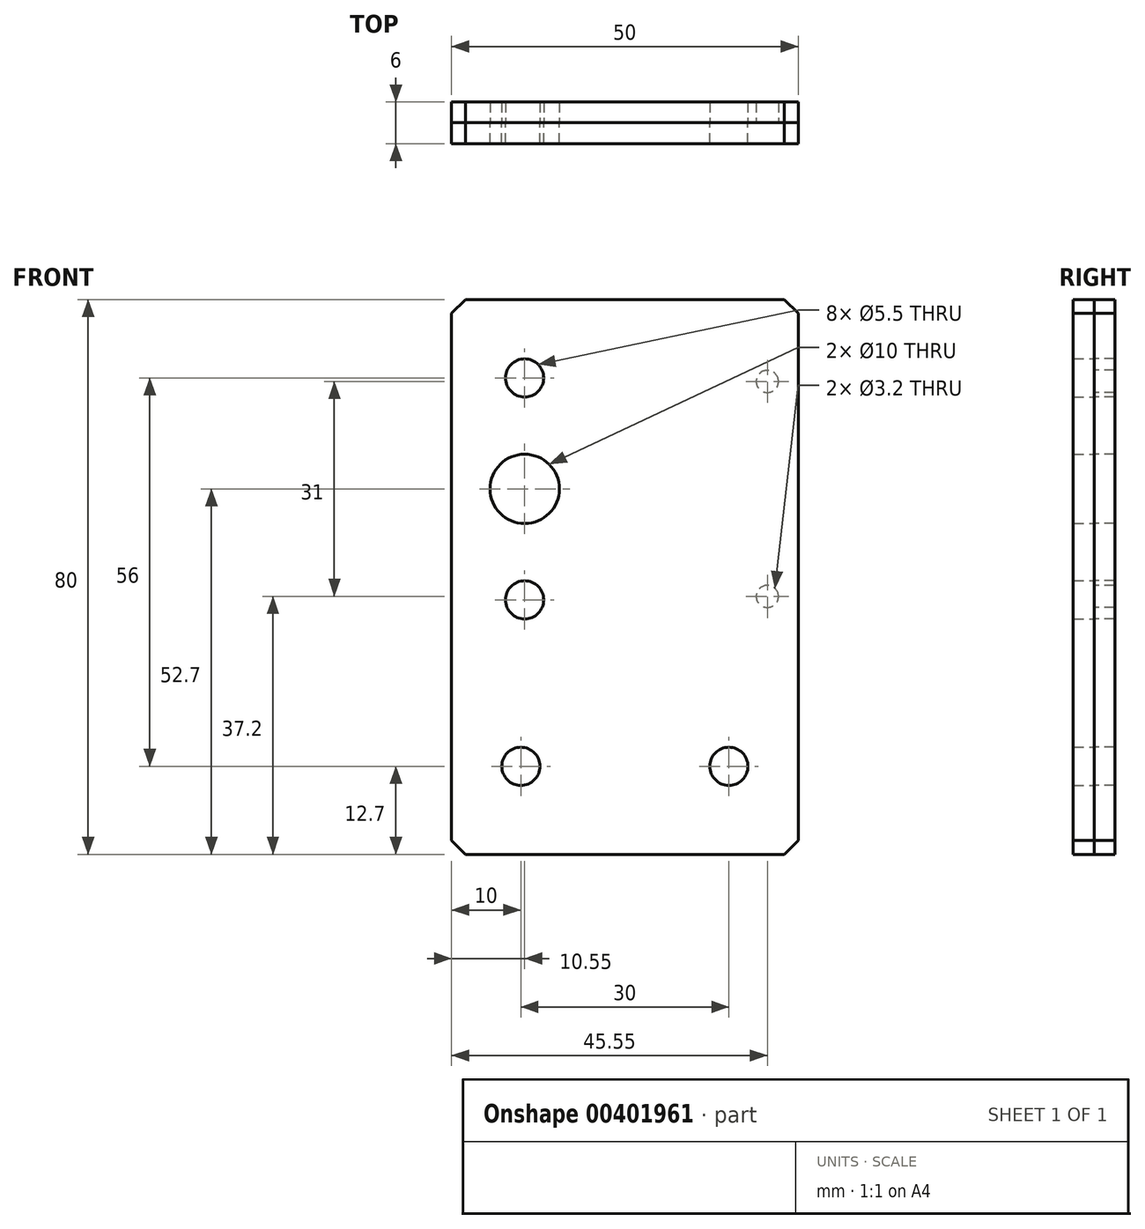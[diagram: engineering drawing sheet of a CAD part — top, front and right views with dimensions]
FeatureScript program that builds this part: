
annotation { "Feature Type Name" : "Feature", "Feature Type Description" : "" }
export const myFeature = defineFeature(function(context is Context, id is Id, definition is map)
    precondition{}
    {
        {
            var Q0;
            Q0=qCreatedBy(makeId("Front.planeOp"),FACE);
            var sketch = newSketch(context, id + "F0", { "sketchPlane" : qUnion([Q0])});
            skLineSegment(sketch, "E0.bottom", {"start": v(-25, 40) * mm, "end": v(25, 40) * mm});
            skLineSegment(sketch, "E0.top", {"start": v(-25, -40) * mm, "end": v(25, -40) * mm});
            skLineSegment(sketch, "E0.left", {"start": v(-25, 40) * mm, "end": v(-25, -40) * mm});
            skLineSegment(sketch, "E0.right", {"start": v(25, 40) * mm, "end": v(25, -40) * mm});
            skLineSegment(sketch, "E1", {"start": v(0, 0) * mm, "end": v(0, 40) * mm, "construction": true});
            skLineSegment(sketch, "E2", {"start": v(0, 0) * mm, "end": v(-25, 0) * mm, "construction": true});
            skSolve(sketch);
        }
        {
            var Q0;
            Q0=makeQuery(id+"F0.imprint","IMPRINT",FACE,{"disambiguationData":[TD([[makeQuery(id+"F0.imprint","IMPRINT",EDGE,{"derivedFrom":sQuery(id+"F0.wireOp",EDGE,"E0.bottom")}),-1.0]])]});
            extrude(context, id + "F1", {"entities" : qUnion([Q0]), "endBound" : BoundingType.SYMMETRIC, "depth" : 3 * mm});
        }
        {
            var Q0;
            Q0=makeQuery(id+"F1.opExtrude","CAP_FACE",FACE,{"disambiguationData":[OSD([sQuery(id+"F0.wireOp",EDGE,"E0.bottom"),sQuery(id+"F0.wireOp",EDGE,"E0.top"),sQuery(id+"F0.wireOp",EDGE,"E0.left"),sQuery(id+"F0.wireOp",EDGE,"E0.right")])],"isStart":false});
            var sketch = newSketch(context, id + "F2", { "sketchPlane" : qUnion([Q0])});
            skLineSegment(sketch, "E3", {"start": v(-25, -14.6) * mm, "end": v(25, -14.6) * mm, "construction": true});
            skPoint(sketch, "E4", {"position": v(-15, -27.3) * mm});
            skPoint(sketch, "E5", {"position": v(15, -27.3) * mm});
            skLineSegment(sketch, "E6", {"start": v(-15, -27.3) * mm, "end": v(15, -27.3) * mm, "construction": true});
            skLineSegment(sketch, "E7", {"start": v(15, -27.3) * mm, "end": v(25, -27.3) * mm, "construction": true});
            skLineSegment(sketch, "E8", {"start": v(-15, -27.3) * mm, "end": v(-25, -27.3) * mm, "construction": true});
            skPoint(sketch, "E9", {"position": v(20.55, 28.2) * mm});
            skPoint(sketch, "E10", {"position": v(20.55, -2.8) * mm});
            skLineSegment(sketch, "E11", {"start": v(20.55, 28.2) * mm, "end": v(20.55, 40) * mm, "construction": true});
            skLineSegment(sketch, "E12", {"start": v(20.55, -2.8) * mm, "end": v(20.55, -14.6) * mm, "construction": true});
            skLineSegment(sketch, "E13", {"start": v(20.55, 28.2) * mm, "end": v(20.55, -2.8) * mm, "construction": true});
            skLineSegment(sketch, "E14", {"start": v(20.55, 12.7) * mm, "end": v(-14.45, 12.7) * mm, "construction": true});
            skLineSegment(sketch, "E15", {"start": v(-14.45, 12.7) * mm, "end": v(-14.45, 28.7) * mm, "construction": true});
            skLineSegment(sketch, "E16", {"start": v(-14.45, 12.7) * mm, "end": v(-14.45, -3.3) * mm, "construction": true});
            skSolve(sketch);
        }
        {
            var Q0;
            Q0=sQuery(id+"F2.wireOp",VERTEX,"E4");
            var Q1;
            Q1=sQuery(id+"F2.wireOp",VERTEX,"E5");
            var Q2;
            Q2=makeQuery(id+"F1.opExtrude","SWEPT_BODY",BODY,{"disambiguationData":[OSD([sQuery(id+"F0.wireOp",EDGE,"E0.bottom"),sQuery(id+"F0.wireOp",EDGE,"E0.top"),sQuery(id+"F0.wireOp",EDGE,"E0.left"),sQuery(id+"F0.wireOp",EDGE,"E0.right")])]});
            hole(context, id + "F3", {"style" : HoleStyle.SIMPLE, "endStyle" : HoleEndStyle.THROUGH, "holeDiameter" : 5.5 * mm, "isTappedThrough" : true, "tappedDepth" : 12 * mm, "tapClearance" : 3, "locations" : qUnion([Q0, Q1]), "scope" : qUnion([Q2])});
        }
        {
            var Q0;
            Q0=sQuery(id+"F2.wireOp",VERTEX,"E9");
            var Q1;
            Q1=sQuery(id+"F2.wireOp",VERTEX,"E10");
            var Q2;
            Q2=makeQuery(id+"F1.opExtrude","SWEPT_BODY",BODY,{"disambiguationData":[OSD([sQuery(id+"F0.wireOp",EDGE,"E0.bottom"),sQuery(id+"F0.wireOp",EDGE,"E0.top"),sQuery(id+"F0.wireOp",EDGE,"E0.left"),sQuery(id+"F0.wireOp",EDGE,"E0.right")])]});
            hole(context, id + "F4", {"style" : HoleStyle.SIMPLE, "endStyle" : HoleEndStyle.THROUGH, "holeDiameter" : 3.2 * mm, "isTappedThrough" : true, "tappedDepth" : 12 * mm, "tapClearance" : 3, "locations" : qUnion([Q0, Q1]), "scope" : qUnion([Q2])});
        }
        {
            var Q0;
            Q0=makeQuery(id+"F1.opExtrude","SWEPT_EDGE",EDGE,{"disambiguationData":[OSD([sQuery(id+"F0.wireOp",EDGE,"E0.bottom"),sQuery(id+"F0.wireOp",EDGE,"E0.left")])]});
            var Q1;
            Q1=makeQuery(id+"F1.opExtrude","SWEPT_EDGE",EDGE,{"disambiguationData":[OSD([sQuery(id+"F0.wireOp",EDGE,"E0.top"),sQuery(id+"F0.wireOp",EDGE,"E0.left")])]});
            var Q2;
            Q2=makeQuery(id+"F1.opExtrude","SWEPT_EDGE",EDGE,{"disambiguationData":[OSD([sQuery(id+"F0.wireOp",EDGE,"E0.bottom"),sQuery(id+"F0.wireOp",EDGE,"E0.right")])]});
            var Q3;
            Q3=makeQuery(id+"F1.opExtrude","SWEPT_EDGE",EDGE,{"disambiguationData":[OSD([sQuery(id+"F0.wireOp",EDGE,"E0.top"),sQuery(id+"F0.wireOp",EDGE,"E0.right")])]});
            chamfer(context, id + "F5", {"entities" : qUnion([Q0, Q1, Q2, Q3]), "width" : 2 * mm, "tangentPropagation" : true});
        }
        {
            var Q0;
            Q0=sQuery(id+"F2.wireOp",VERTEX,"E15.end");
            var Q1;
            Q1=sQuery(id+"F2.wireOp",VERTEX,"E16.end");
            var Q2;
            Q2=makeQuery(id+"F1.opExtrude","SWEPT_BODY",BODY,{"disambiguationData":[OSD([sQuery(id+"F0.wireOp",EDGE,"E0.bottom"),sQuery(id+"F0.wireOp",EDGE,"E0.top"),sQuery(id+"F0.wireOp",EDGE,"E0.left"),sQuery(id+"F0.wireOp",EDGE,"E0.right")])]});
            hole(context, id + "F6", {"style" : HoleStyle.SIMPLE, "endStyle" : HoleEndStyle.THROUGH, "holeDiameter" : 5.5 * mm, "isTappedThrough" : true, "tappedDepth" : 12 * mm, "tapClearance" : 3, "locations" : qUnion([Q0, Q1]), "scope" : qUnion([Q2])});
        }
        {
            var Q0;
            Q0=sQuery(id+"F2.wireOp",VERTEX,"E15.start");
            var Q1;
            Q1=makeQuery(id+"F1.opExtrude","SWEPT_BODY",BODY,{"disambiguationData":[OSD([sQuery(id+"F0.wireOp",EDGE,"E0.bottom"),sQuery(id+"F0.wireOp",EDGE,"E0.top"),sQuery(id+"F0.wireOp",EDGE,"E0.left"),sQuery(id+"F0.wireOp",EDGE,"E0.right")])]});
            hole(context, id + "F7", {"style" : HoleStyle.SIMPLE, "endStyle" : HoleEndStyle.THROUGH, "holeDiameter" : 10 * mm, "isTappedThrough" : true, "tappedDepth" : 12 * mm, "tapClearance" : 3, "locations" : qUnion([Q0]), "scope" : qUnion([Q1])});
        }
        {
            var Q0;
            Q0=makeQuery(id+"F2.imprint","IMPRINT",FACE,{"disambiguationData":[TD([[makeQuery(id+"F2.imprint","IMPRINT",EDGE,{"derivedFrom":makeQuery(id+"F1.opExtrude","CAP_EDGE",EDGE,{"disambiguationData":[OSD([sQuery(id+"F0.wireOp",EDGE,"E0.bottom")])],"isStart":false})}),-1.0]])]});
            extrude(context, id + "F8", {"entities" : qUnion([Q0]), "depth" : 3 * mm});
        }
        {
            var Q0;
            Q0=makeQuery(id+"F8.opExtrude","SWEPT_EDGE",EDGE,{"disambiguationData":[OSD([sQuery(id+"F0.wireOp",EDGE,"E0.bottom"),sQuery(id+"F0.wireOp",EDGE,"E0.right")])]});
            var Q1;
            Q1=makeQuery(id+"F8.opExtrude","SWEPT_EDGE",EDGE,{"disambiguationData":[OSD([sQuery(id+"F0.wireOp",EDGE,"E0.bottom"),sQuery(id+"F0.wireOp",EDGE,"E0.left")])]});
            var Q2;
            Q2=makeQuery(id+"F8.opExtrude","SWEPT_EDGE",EDGE,{"disambiguationData":[OSD([sQuery(id+"F0.wireOp",EDGE,"E0.top"),sQuery(id+"F0.wireOp",EDGE,"E0.right")])]});
            var Q3;
            Q3=makeQuery(id+"F8.opExtrude","SWEPT_EDGE",EDGE,{"disambiguationData":[OSD([sQuery(id+"F0.wireOp",EDGE,"E0.top"),sQuery(id+"F0.wireOp",EDGE,"E0.left")])]});
            chamfer(context, id + "F9", {"entities" : qUnion([Q0, Q1, Q2, Q3]), "width" : 2 * mm, "tangentPropagation" : true});
        }
        {
            var Q0;
            Q0=sQuery(id+"F2.wireOp",VERTEX,"E5");
            var Q1;
            Q1=sQuery(id+"F2.wireOp",VERTEX,"E4");
            var Q2;
            Q2=makeQuery(id+"F8.opExtrude","SWEPT_BODY",BODY,{"disambiguationData":[OSD([sQuery(id+"F0.wireOp",EDGE,"E0.bottom"),sQuery(id+"F0.wireOp",EDGE,"E0.top"),sQuery(id+"F0.wireOp",EDGE,"E0.left"),sQuery(id+"F0.wireOp",EDGE,"E0.right")])]});
            hole(context, id + "F10", {"style" : HoleStyle.SIMPLE, "endStyle" : HoleEndStyle.THROUGH, "oppositeDirection" : true, "holeDiameter" : 5.5 * mm, "isTappedThrough" : true, "tappedDepth" : 12 * mm, "tapClearance" : 3, "locations" : qUnion([Q0, Q1]), "scope" : qUnion([Q2])});
        }
        {
            var Q0;
            Q0=sQuery(id+"F2.wireOp",VERTEX,"E15.end");
            var Q1;
            Q1=sQuery(id+"F2.wireOp",VERTEX,"E16.end");
            var Q2;
            Q2=makeQuery(id+"F8.opExtrude","SWEPT_BODY",BODY,{"disambiguationData":[OSD([sQuery(id+"F0.wireOp",EDGE,"E0.bottom"),sQuery(id+"F0.wireOp",EDGE,"E0.top"),sQuery(id+"F0.wireOp",EDGE,"E0.left"),sQuery(id+"F0.wireOp",EDGE,"E0.right")])]});
            hole(context, id + "F11", {"style" : HoleStyle.SIMPLE, "endStyle" : HoleEndStyle.THROUGH, "oppositeDirection" : true, "holeDiameter" : 5.5 * mm, "isTappedThrough" : true, "tappedDepth" : 12 * mm, "tapClearance" : 3, "locations" : qUnion([Q0, Q1]), "scope" : qUnion([Q2])});
        }
        {
            var Q0;
            Q0=sQuery(id+"F2.wireOp",VERTEX,"E15.start");
            var Q1;
            Q1=makeQuery(id+"F8.opExtrude","SWEPT_BODY",BODY,{"disambiguationData":[OSD([sQuery(id+"F0.wireOp",EDGE,"E0.bottom"),sQuery(id+"F0.wireOp",EDGE,"E0.top"),sQuery(id+"F0.wireOp",EDGE,"E0.left"),sQuery(id+"F0.wireOp",EDGE,"E0.right")])]});
            hole(context, id + "F12", {"style" : HoleStyle.SIMPLE, "endStyle" : HoleEndStyle.THROUGH, "oppositeDirection" : true, "holeDiameter" : 10 * mm, "isTappedThrough" : true, "tappedDepth" : 12 * mm, "tapClearance" : 3, "locations" : qUnion([Q0]), "scope" : qUnion([Q1])});
        }
    });
